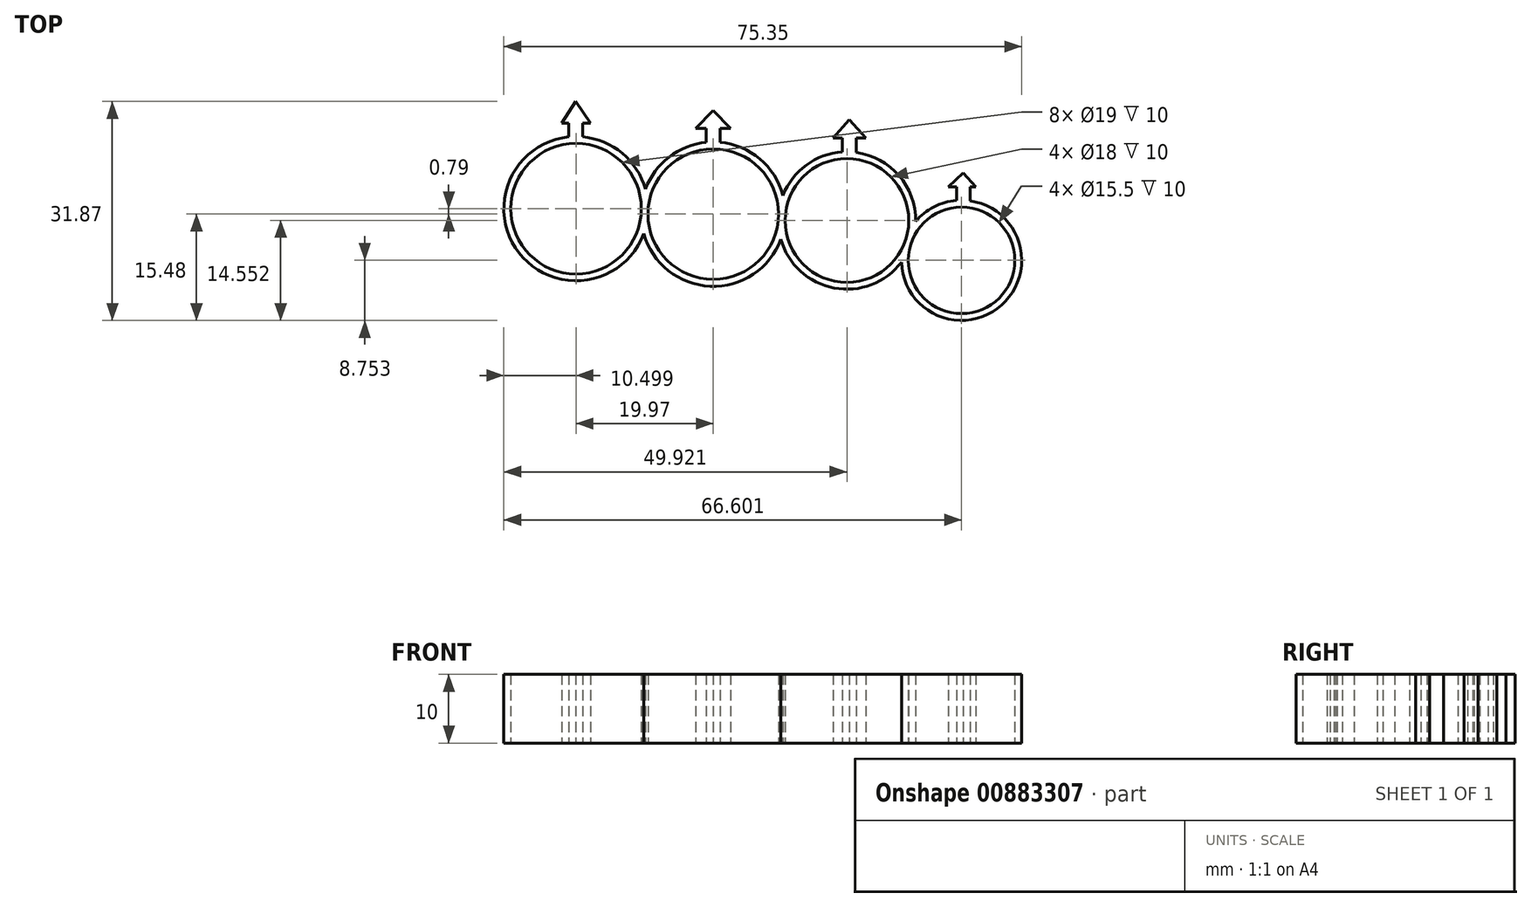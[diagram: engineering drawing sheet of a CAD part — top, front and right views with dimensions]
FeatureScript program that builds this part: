
annotation { "Feature Type Name" : "Feature", "Feature Type Description" : "" }
export const myFeature = defineFeature(function(context is Context, id is Id, definition is map)
    precondition{}
    {
        {
            var Q0;
            Q0=qCreatedBy(makeId("Top.planeOp"),FACE);
            var sketch = newSketch(context, id + "F0", { "sketchPlane" : qUnion([Q0])});
            skCircle(sketch, "E0", {"center": v(-63.63, 34.75) * mm, "radius": 9.5 * mm});
            skCircle(sketch, "E1", {"center": v(-43.66, 33.96) * mm, "radius": 9.5 * mm});
            skCircle(sketch, "E2", {"center": v(-24.2, 33.03) * mm, "radius": 9 * mm});
            skCircle(sketch, "E3", {"center": v(-7.53, 27.23) * mm, "radius": 7.75 * mm});
            skCircle(sketch, "E4", {"center": v(-63.63, 34.75) * mm, "radius": 10.5 * mm});
            skCircle(sketch, "E5", {"center": v(-43.66, 33.96) * mm, "radius": 10.5 * mm});
            skCircle(sketch, "E6", {"center": v(-24.2, 33.03) * mm, "radius": 10 * mm});
            skCircle(sketch, "E7", {"center": v(-7.53, 27.23) * mm, "radius": 8.75 * mm});
            skLineSegment(sketch, "E8", {"start": v(-64.68, 45.2) * mm, "end": v(-64.68, 47.2) * mm});
            skLineSegment(sketch, "E9", {"start": v(-64.68, 47.2) * mm, "end": v(-62.68, 47.2) * mm});
            skLineSegment(sketch, "E10", {"start": v(-62.68, 47.2) * mm, "end": v(-62.68, 45.2) * mm});
            skLineSegment(sketch, "E11", {"start": v(-44.67, 44.41) * mm, "end": v(-44.67, 46.41) * mm});
            skLineSegment(sketch, "E12", {"start": v(-44.67, 46.41) * mm, "end": v(-42.67, 46.41) * mm});
            skLineSegment(sketch, "E13", {"start": v(-42.67, 46.41) * mm, "end": v(-42.67, 44.41) * mm});
            skLineSegment(sketch, "E14", {"start": v(-42.67, 44.41) * mm, "end": v(-42.67, 46.41) * mm});
            skLineSegment(sketch, "E15", {"start": v(-24.87, 43) * mm, "end": v(-24.87, 45) * mm});
            skLineSegment(sketch, "E16", {"start": v(-24.87, 45) * mm, "end": v(-22.87, 45.07) * mm});
            skLineSegment(sketch, "E17", {"start": v(-22.87, 45.07) * mm, "end": v(-22.87, 42.94) * mm});
            skLineSegment(sketch, "E18", {"start": v(-22.87, 42.94) * mm, "end": v(-22.87, 45.07) * mm});
            skLineSegment(sketch, "E19", {"start": v(-8.27, 35.95) * mm, "end": v(-8.27, 37.95) * mm});
            skLineSegment(sketch, "E20", {"start": v(-8.27, 37.95) * mm, "end": v(-6.27, 37.95) * mm});
            skLineSegment(sketch, "E21", {"start": v(-6.27, 37.95) * mm, "end": v(-6.27, 35.9) * mm});
            skLineSegment(sketch, "E22", {"start": v(-64.68, 47.2) * mm, "end": v(-65.72, 47.2) * mm});
            skLineSegment(sketch, "E23", {"start": v(-65.72, 47.2) * mm, "end": v(-63.68, 50.35) * mm});
            skPoint(sketch, "E23.endSnap0", {"position": v(-63.68, 47.2) * mm});
            skLineSegment(sketch, "E24", {"start": v(-63.68, 50.35) * mm, "end": v(-61.49, 47.2) * mm});
            skLineSegment(sketch, "E25", {"start": v(-61.49, 47.2) * mm, "end": v(-62.68, 47.2) * mm});
            skLineSegment(sketch, "E26", {"start": v(-44.67, 46.41) * mm, "end": v(-46.2, 46.41) * mm});
            skLineSegment(sketch, "E27", {"start": v(-46.2, 46.41) * mm, "end": v(-43.67, 49.02) * mm});
            skPoint(sketch, "E27.endSnap0", {"position": v(-43.67, 46.41) * mm});
            skLineSegment(sketch, "E28", {"start": v(-43.67, 49.02) * mm, "end": v(-41.14, 46.41) * mm});
            skLineSegment(sketch, "E29", {"start": v(-41.14, 46.41) * mm, "end": v(-42.67, 46.41) * mm});
            skLineSegment(sketch, "E30", {"start": v(-24.87, 45) * mm, "end": v(-26.2, 45) * mm});
            skLineSegment(sketch, "E31", {"start": v(-26.2, 45) * mm, "end": v(-23.87, 47.7) * mm});
            skPoint(sketch, "E31.endSnap0", {"position": v(-23.87, 45.04) * mm});
            skLineSegment(sketch, "E32", {"start": v(-23.87, 47.7) * mm, "end": v(-21.48, 45) * mm});
            skLineSegment(sketch, "E33", {"start": v(-21.48, 45) * mm, "end": v(-22.87, 45.07) * mm});
            skLineSegment(sketch, "E34", {"start": v(-8.27, 37.95) * mm, "end": v(-9.45, 37.95) * mm});
            skLineSegment(sketch, "E35", {"start": v(-9.45, 37.95) * mm, "end": v(-7.27, 39.94) * mm});
            skPoint(sketch, "E35.endSnap0", {"position": v(-7.27, 37.95) * mm});
            skLineSegment(sketch, "E36", {"start": v(-7.27, 39.94) * mm, "end": v(-5.46, 37.95) * mm});
            skLineSegment(sketch, "E37", {"start": v(-5.46, 37.95) * mm, "end": v(-6.27, 37.95) * mm});
            skSolve(sketch);
        }
        {
            var Q0;
            Q0 = qSketchRegion(id + "F0", true);
            extrude(context, id + "F1", {"entities" : qUnion([Q0]), "depth" : 10 * mm, "offsetDistance" : 25.4 * mm});
        }
    });
